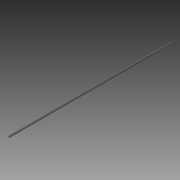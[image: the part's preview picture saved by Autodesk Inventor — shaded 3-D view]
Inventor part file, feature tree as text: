
AUTODESK INVENTOR PART (.ipt)
format: ipt  version: 2013 (Build 170138000, 138)  size: 64,000 bytes
history: native  units: in
note: dims shown in document units (in); Inventor stores cm internally (conversion verified against a paired STEP export)
features: extrude x1, thread x1, sketch x1
ambient origin geometry x8: Origin, YZ Plane, XZ Plane, XY Plane, X Axis, Y Axis, Z Axis, Center Point
bodies: Solid1 (feature_tree)
feature tree (3):
  extrude  "Extrusion1"  Depth=27.7559in TaperAngle=0.0deg
  thread  "Thread1"  [1 undecoded]
  sketch  "Sketch1"  dims[d0=0.315in d2=27.7559in d3=0.0in d4=1.0in d5=0.0in]
note: 1 required parameter value undecoded (feature->parameter linkage not recoverable at this tier; creation-order binding heuristic only, values carry confidence <= 0.55)
